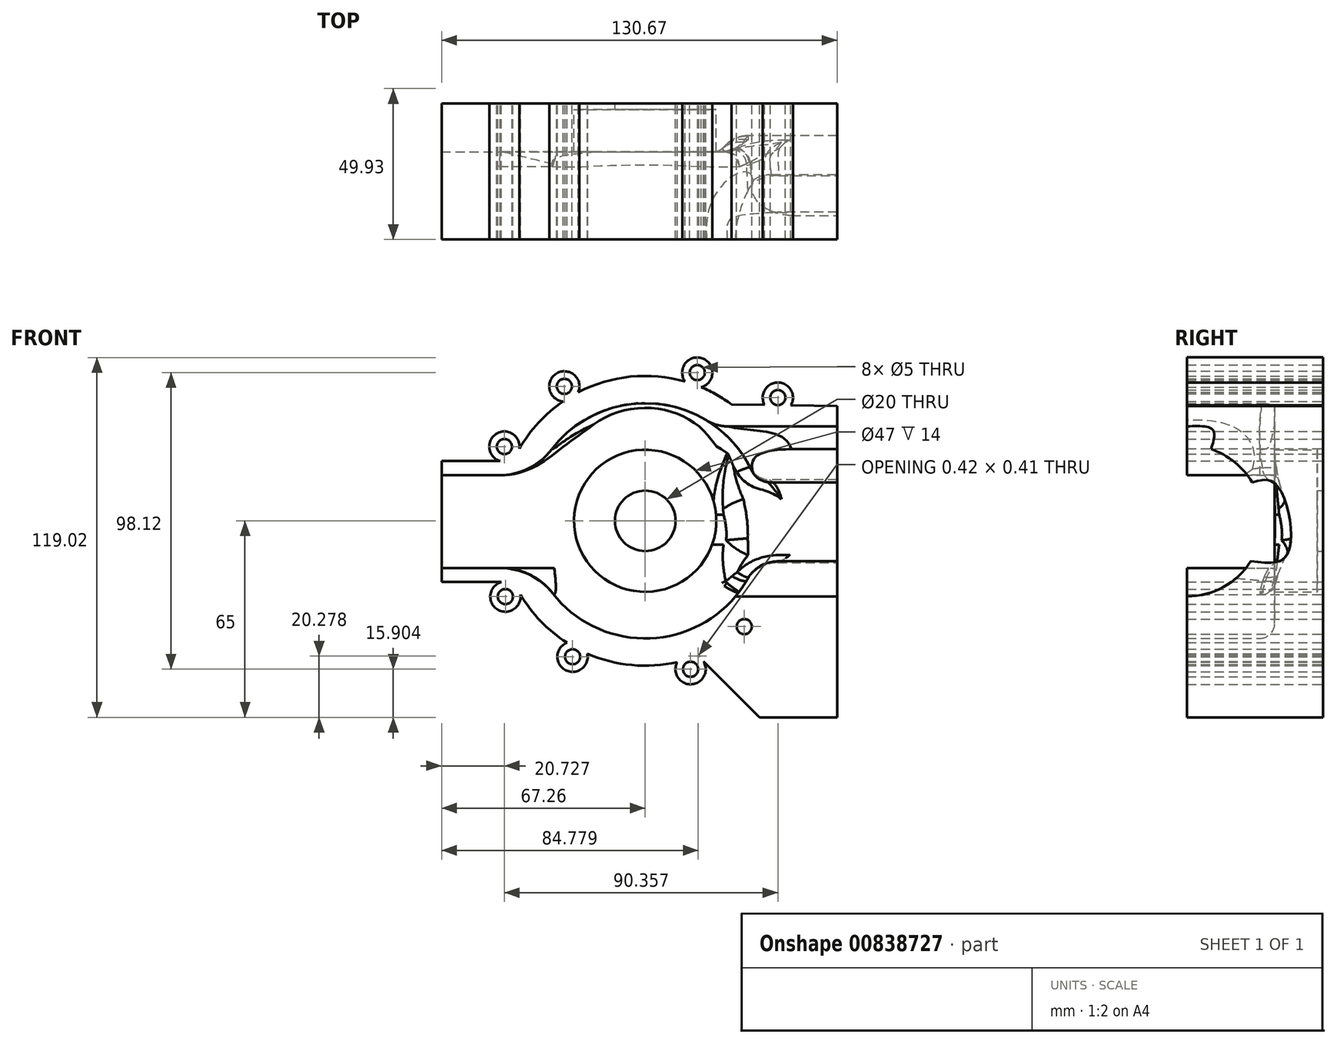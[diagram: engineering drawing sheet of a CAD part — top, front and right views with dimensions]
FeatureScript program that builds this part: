
annotation { "Feature Type Name" : "Feature", "Feature Type Description" : "" }
export const myFeature = defineFeature(function(context is Context, id is Id, definition is map)
    precondition{}
    {
        {
            var Q0;
            Q0=qCreatedBy(makeId("Front.planeOp"),FACE);
            var sketch = newSketch(context, id + "F0", { "sketchPlane" : qUnion([Q0])});
            skCircle(sketch, "E0", {"center": v(0, 0) * mm, "radius": 10 * mm});
            skCircle(sketch, "E1", {"center": v(0, 0) * mm, "radius": 23.5 * mm});
            skCircle(sketch, "E2", {"center": v(0, 0) * mm, "radius": 38.9 * mm});
            skLineSegment(sketch, "E3", {"start": v(-67.26, 19.74) * mm, "end": v(-33.52, 19.74) * mm});
            skLineSegment(sketch, "E4", {"start": v(-67.26, 19.74) * mm, "end": v(-67.26, -20.26) * mm});
            skLineSegment(sketch, "E5", {"start": v(-33.2, -20.26) * mm, "end": v(-67.26, -20.26) * mm});
            skArc(sketch, "E6", {"start": v(-43.42, -20.26) * mm, "mid": v(47.92, 0.28) * mm, "end": v(-43.66, 19.74) * mm});
            skLineSegment(sketch, "E7", {"start": v(-67.26, 15.06) * mm, "end": v(-35.87, 15.06) * mm});
            skLineSegment(sketch, "E8", {"start": v(-67.26, -15.65) * mm, "end": v(-35.61, -15.65) * mm});
            skLineSegment(sketch, "E9", {"start": v(28.53, 38.5) * mm, "end": v(63.41, 38) * mm});
            skLineSegment(sketch, "E10", {"start": v(63.41, 38) * mm, "end": v(63.41, -35) * mm});
            skLineSegment(sketch, "E11", {"start": v(63.41, -35) * mm, "end": v(32.73, -35) * mm});
            skLineSegment(sketch, "E12.bottom", {"start": v(28.66, 26.62) * mm, "end": v(63.41, 26.62) * mm});
            skLineSegment(sketch, "E12.top", {"start": v(31.09, -23.38) * mm, "end": v(63.41, -23.38) * mm});
            skLineSegment(sketch, "E12.left", {"start": v(28.66, 26.62) * mm, "end": v(28.66, 26.3) * mm});
            skPoint(sketch, "E12.middle", {"position": v(63.41, 1.5) * mm});
            skArc(sketch, "E13", {"start": v(-25.89, -40.32) * mm, "mid": v(-26.37, -49.37) * mm, "end": v(-19.12, -43.94) * mm});
            skArc(sketch, "E14", {"start": v(10.6, -46.73) * mm, "mid": v(16.45, -53.87) * mm, "end": v(17.3, -44.68) * mm});
            skArc(sketch, "E15", {"start": v(-47.54, -20.26) * mm, "mid": v(-48.95, -29.26) * mm, "end": v(-41.26, -24.37) * mm});
            skArc(sketch, "E16", {"start": v(-41.59, 23.8) * mm, "mid": v(-49.22, 28.76) * mm, "end": v(-47.95, 19.74) * mm});
            skArc(sketch, "E17", {"start": v(-22.12, 42.5) * mm, "mid": v(-29.3, 48.75) * mm, "end": v(-27.16, 39.47) * mm});
            skArc(sketch, "E18", {"start": v(18.5, 44.2) * mm, "mid": v(18.85, 53.74) * mm, "end": v(13.16, 46.07) * mm});
            skArc(sketch, "E19", {"start": v(48.14, 38.22) * mm, "mid": v(43.9, 45.75) * mm, "end": v(39.44, 38.34) * mm});
            skSolve(sketch);
        }
        {
            var Q0;
            Q0=makeQuery(id+"F0.imprint","IMPRINT",FACE,{"disambiguationData":[TD([[makeQuery(id+"F0.imprint","IMPRINT",EDGE,{"derivedFrom":sQuery(id+"F0.wireOp",EDGE,"E0")}),-1.0]])]});
            extrude(context, id + "F1", {"entities" : qUnion([Q0]), "depth" : 2 * mm, "offsetDistance" : 25 * mm});
        }
        {
            var Q0;
            Q0=makeQuery(id+"F0.imprint","IMPRINT",FACE,{"disambiguationData":[TD([[makeQuery(id+"F0.imprint","IMPRINT",EDGE,{"derivedFrom":sQuery(id+"F0.wireOp",EDGE,"E1")}),-1.0]])]});
            extrude(context, id + "F2", {"entities" : qUnion([Q0]), "operationType" : NewBodyOperationType.ADD, "depth" : 16 * mm, "offsetDistance" : 25 * mm});
        }
        {
            var Q0;
            {var subQ8=sQuery(id+"F0.wireOp",EDGE,"E12.left");Q0=makeQuery(id+"F0.imprint","IMPRINT",FACE,{"disambiguationData":[TD([[makeQuery(id+"F0.imprint","IMPRINT",EDGE,{"derivedFrom":subQ8}),-1.0]])]});}
            var Q1;
            {var subQ1=sQuery(id+"F0.wireOp",EDGE,"E5");var subQ4=sQuery(id+"F0.wireOp",EDGE,"E2");var subQ5=makeQuery(id+"F0.imprint","INTERSECT",VERTEX,{"derivedFrom":[subQ4,subQ1]});Q1=makeQuery(id+"F0.imprint","IMPRINT",FACE,{"disambiguationData":[TD([[makeQuery(id+"F0.imprint","IMPRINT",EDGE,{"disambiguationData":[TD([[subQ5,-1.0]])],"derivedFrom":subQ4}),-1.0]])]});}
            var Q2;
            {var subQ3=sQuery(id+"F0.wireOp",EDGE,"E7");Q2=makeQuery(id+"F0.imprint","IMPRINT",FACE,{"disambiguationData":[TD([[makeQuery(id+"F0.imprint","IMPRINT",EDGE,{"derivedFrom":subQ3}),1.0]])]});}
            var Q3;
            {var subQ6=sQuery(id+"F0.wireOp",EDGE,"E8");Q3=makeQuery(id+"F0.imprint","IMPRINT",FACE,{"disambiguationData":[TD([[makeQuery(id+"F0.imprint","IMPRINT",EDGE,{"derivedFrom":subQ6}),-1.0]])]});}
            var Q4;
            {var subQ0=sQuery(id+"F0.wireOp",EDGE,"E11");Q4=makeQuery(id+"F0.imprint","IMPRINT",FACE,{"disambiguationData":[TD([[makeQuery(id+"F0.imprint","IMPRINT",EDGE,{"derivedFrom":subQ0}),-1.0]])]});}
            var Q5;
            {var subQ0=sQuery(id+"F0.wireOp",EDGE,"E9");Q5=makeQuery(id+"F0.imprint","IMPRINT",FACE,{"disambiguationData":[TD([[makeQuery(id+"F0.imprint","IMPRINT",EDGE,{"derivedFrom":subQ0}),-1.0]])]});}
            extrude(context, id + "F3", {"entities" : qUnion([Q0, Q1, Q2, Q3, Q4, Q5]), "operationType" : NewBodyOperationType.ADD, "depth" : 35 * mm, "offsetDistance" : 25 * mm});
        }
        {
            var Q0;
            {var subQ0=sQuery(id+"F0.wireOp",EDGE,"E7");Q0=makeQuery(id+"F0.imprint","IMPRINT",FACE,{"disambiguationData":[TD([[makeQuery(id+"F0.imprint","IMPRINT",EDGE,{"derivedFrom":subQ0}),-1.0]])]});}
            var Q1;
            {var subQ0=sQuery(id+"F0.wireOp",EDGE,"E12.top");var subQ1=sQuery(id+"F0.wireOp",EDGE,"E6");var subQ2=makeQuery(id+"F0.imprint","INTERSECT",VERTEX,{"derivedFrom":[subQ1,subQ0]});Q1=makeQuery(id+"F0.imprint","IMPRINT",FACE,{"disambiguationData":[TD([[makeQuery(id+"F0.imprint","IMPRINT",EDGE,{"disambiguationData":[TD([[subQ2,-1.0]])],"derivedFrom":subQ1}),-1.0]])]});}
            var Q2;
            {var subQ5=sQuery(id+"F0.wireOp",EDGE,"E12.left");Q2=makeQuery(id+"F0.imprint","IMPRINT",FACE,{"disambiguationData":[TD([[makeQuery(id+"F0.imprint","IMPRINT",EDGE,{"derivedFrom":subQ5}),1.0]])]});}
            extrude(context, id + "F4", {"entities" : qUnion([Q0, Q1, Q2]), "operationType" : NewBodyOperationType.ADD, "depth" : 16 * mm, "offsetDistance" : 25 * mm});
        }
        {
            var Q0;
            Q0=makeQuery(id+"F3.opExtrude","SWEPT_FACE",FACE,{"disambiguationData":[OSD([sQuery(id+"F0.wireOp",EDGE,"E11")])]});
            extrude(context, id + "F5", {"entities" : qUnion([Q0]), "operationType" : NewBodyOperationType.ADD, "depth" : 30 * mm, "offsetDistance" : 25 * mm});
        }
        {
            var Q0;
            Q0=makeQuery(id+"F5.opExtrude","SWEPT_FACE",FACE,{"disambiguationData":[OSD([sQuery(id+"F0.wireOp",EDGE,"E6"),sQuery(id+"F0.wireOp",EDGE,"E11")])]});
            extrude(context, id + "F6", {"entities" : qUnion([Q0]), "operationType" : NewBodyOperationType.ADD, "depth" : 15 * mm, "offsetDistance" : 25 * mm});
        }
        {
            var Q0;
            {var subQ0=sQuery(id+"F0.wireOp",EDGE,"E11");var subQ1=sQuery(id+"F0.wireOp",EDGE,"E6");Q0=makeQuery(id+"F6.opExtrude","CAP_EDGE",EDGE,{"disambiguationData":[OSD([subQ1,subQ0]),TDD([makeQuery(id+"F5.opExtrude","CAP_EDGE",EDGE,{"disambiguationData":[OSD([subQ1,subQ0])],"isStart":false})])],"isStart":false});}
            chamfer(context, id + "F7", {"entities" : qUnion([Q0]), "width" : 20 * mm, "tangentPropagation" : true});
        }
        {
            var Q0;
            {var subQ5=sQuery(id+"F0.wireOp",EDGE,"E12.left");Q0=makeQuery(id+"F0.imprint","IMPRINT",FACE,{"disambiguationData":[TD([[makeQuery(id+"F0.imprint","IMPRINT",EDGE,{"derivedFrom":subQ5}),1.0]])]});}
            var Q1;
            {var subQ0=sQuery(id+"F0.wireOp",EDGE,"E12.top");var subQ1=sQuery(id+"F0.wireOp",EDGE,"E6");var subQ2=makeQuery(id+"F0.imprint","INTERSECT",VERTEX,{"derivedFrom":[subQ1,subQ0]});Q1=makeQuery(id+"F0.imprint","IMPRINT",FACE,{"disambiguationData":[TD([[makeQuery(id+"F0.imprint","IMPRINT",EDGE,{"disambiguationData":[TD([[subQ2,-1.0]])],"derivedFrom":subQ1}),-1.0]])]});}
            extrude(context, id + "F8", {"entities" : qUnion([Q0, Q1]), "operationType" : NewBodyOperationType.ADD, "depth" : 35 * mm, "offsetDistance" : 25 * mm});
        }
        {
            var Q0;
            {var subQ0=sQuery(id+"F0.wireOp",EDGE,"E12.left");var subQ1=sQuery(id+"F0.wireOp",EDGE,"E12.top");var subQ2=sQuery(id+"F0.wireOp",EDGE,"E12.bottom");var subQ3=sQuery(id+"F0.wireOp",EDGE,"E10");var subQ4=sQuery(id+"F0.wireOp",EDGE,"E2");var subQ5=sQuery(id+"F0.wireOp",EDGE,"E11");var subQ6=sQuery(id+"F0.wireOp",EDGE,"E6");var subQ7=sQuery(id+"F0.wireOp",EDGE,"E4");Q0=makeQuery(id+"F8.boolean.opBoolean","MERGE",FACE,{"derivedFrom":[makeQuery(id+"F3.opExtrude","CAP_FACE",FACE,{"disambiguationData":[OSD([subQ4,sQuery(id+"F0.wireOp",EDGE,"E3"),subQ7,subQ6,sQuery(id+"F0.wireOp",EDGE,"E7"),sQuery(id+"F0.wireOp",EDGE,"E9"),subQ3,subQ2,subQ0])],"isStart":false}),makeQuery(id+"F6.boolean.opBoolean","MERGE",FACE,{"derivedFrom":[makeQuery(id+"F5.boolean.opBoolean","MERGE",FACE,{"derivedFrom":[makeQuery(id+"F3.opExtrude","CAP_FACE",FACE,{"disambiguationData":[OSD([subQ4,subQ7,sQuery(id+"F0.wireOp",EDGE,"E5"),subQ6,sQuery(id+"F0.wireOp",EDGE,"E8"),subQ3,subQ5,subQ1])],"isStart":false}),makeQuery(id+"F5.opExtrude","SWEPT_FACE",FACE,{"disambiguationData":[OSD([subQ5]),TDD([makeQuery(id+"F3.opExtrude","CAP_EDGE",EDGE,{"disambiguationData":[OSD([subQ5])],"isStart":false})])]})]}),makeQuery(id+"F6.opExtrude","SWEPT_FACE",FACE,{"disambiguationData":[OSD([subQ6,subQ5]),TDD([makeQuery(id+"F5.opExtrude","SWEPT_EDGE",EDGE,{"disambiguationData":[OSD([subQ6,subQ5]),TDD([makeQuery(id+"F3.opExtrude","CAP_VERTEX",VERTEX,{"disambiguationData":[OSD([subQ6,subQ5])],"isStart":false})])]})])]})]}),makeQuery(id+"F8.opExtrude","CAP_FACE",FACE,{"disambiguationData":[OSD([subQ4,subQ3,subQ2,subQ1,subQ0])],"isStart":false})]});}
            extrude(context, id + "F9", {"entities" : qUnion([Q0]), "operationType" : NewBodyOperationType.ADD, "depth" : 10 * mm, "offsetDistance" : 25 * mm});
        }
        {
            var Q0;
            {var subQ0=sQuery(id+"F0.wireOp",EDGE,"E11");var subQ1=sQuery(id+"F0.wireOp",EDGE,"E10");Q0=makeQuery(id+"F9.boolean.opBoolean","MERGE",FACE,{"derivedFrom":[makeQuery(id+"F8.boolean.opBoolean","MERGE",FACE,{"derivedFrom":[makeQuery(id+"F5.boolean.opBoolean","MERGE",FACE,{"derivedFrom":[makeQuery(id+"F4.boolean.opBoolean","MERGE",FACE,{"derivedFrom":[makeQuery(id+"F3.opExtrude","SWEPT_FACE",FACE,{"disambiguationData":[OSD([subQ1]),TDD([makeQuery(id+"F0.imprint","IMPRINT",EDGE,{"disambiguationData":[TD([[makeQuery(id+"F0.imprint","INTERSECT",VERTEX,{"derivedFrom":[sQuery(id+"F0.wireOp",EDGE,"E9"),subQ1]}),-1.0]])],"derivedFrom":subQ1})])]}),makeQuery(id+"F3.opExtrude","SWEPT_FACE",FACE,{"disambiguationData":[OSD([subQ1]),TDD([makeQuery(id+"F0.imprint","IMPRINT",EDGE,{"disambiguationData":[TD([[makeQuery(id+"F0.imprint","INTERSECT",VERTEX,{"derivedFrom":[subQ1,subQ0]}),1.0]])],"derivedFrom":subQ1})])]}),makeQuery(id+"F4.opExtrude","SWEPT_FACE",FACE,{"disambiguationData":[OSD([subQ1])]})]}),makeQuery(id+"F5.opExtrude","SWEPT_FACE",FACE,{"disambiguationData":[OSD([subQ1,subQ0])]})]}),makeQuery(id+"F8.opExtrude","SWEPT_FACE",FACE,{"disambiguationData":[OSD([subQ1])]})]}),makeQuery(id+"F9.opExtrude","SWEPT_FACE",FACE,{"disambiguationData":[OSD([subQ1,subQ0])]})]});}
            var sketch = newSketch(context, id + "F10", { "sketchPlane" : qUnion([Q0])});
            skArc(sketch, "E20", {"start": v(-23.46, 12.69) * mm, "mid": v(-32.6, 21.7) * mm, "end": v(-45, 25) * mm});
            skFitSpline(sketch, "E21", {"points": [v(-23.46, 12.69) * mm, v(-16.54, 12.88) * mm, v(-11, 0) * mm, v(-12.98, -12.48) * mm, v(-23.87, -13.36) * mm], "startDerivative": vector(40.87, 11.17) * mm, "endDerivative": vector(-55.8, 6.66) * mm});
            skFitSpline(sketch, "E22", {"points": [v(-37.04, 23.7) * mm, v(-36.44, 30.03) * mm, v(-45, 31.24) * mm], "startDerivative": vector(5.27, 16.32) * mm, "endDerivative": vector(-20.53, -0.83) * mm});
            skLineSegment(sketch, "E23", {"start": v(-45, 31.24) * mm, "end": v(-45, 25) * mm});
            skArc(sketch, "E24", {"start": v(-45, -25) * mm, "mid": v(-20, 0) * mm, "end": v(-45, 25) * mm});
            skLineSegment(sketch, "E25", {"start": v(-45, 25) * mm, "end": v(-45, -25) * mm});
            skArc(sketch, "E26.trimOffspring", {"start": v(-45, -25) * mm, "mid": v(-32.94, -21.9) * mm, "end": v(-23.87, -13.36) * mm});
            skSolve(sketch);
        }
        {
            var Q0;
            {var subQ0=sQuery(id+"F10.wireOp",EDGE,"E25");Q0=makeQuery(id+"F10.imprint","IMPRINT",FACE,{"disambiguationData":[TD([[makeQuery(id+"F10.imprint","IMPRINT",EDGE,{"derivedFrom":subQ0}),1.0]])]});}
            extrude(context, id + "F11", {"entities" : qUnion([Q0]), "operationType" : NewBodyOperationType.REMOVE, "oppositeDirection" : true, "depth" : 51.1 * mm, "offsetDistance" : 25 * mm});
        }
        {
            var Q0;
            {var subQ0=sQuery(id+"F10.wireOp",EDGE,"E21");Q0=makeQuery(id+"F10.imprint","IMPRINT",FACE,{"disambiguationData":[TD([[makeQuery(id+"F10.imprint","IMPRINT",EDGE,{"derivedFrom":subQ0}),-1.0]])]});}
            var Q1;
            {var subQ0=sQuery(id+"F10.wireOp",EDGE,"E22");Q1=makeQuery(id+"F10.imprint","IMPRINT",FACE,{"disambiguationData":[TD([[makeQuery(id+"F10.imprint","IMPRINT",EDGE,{"derivedFrom":subQ0}),1.0]])]});}
            extrude(context, id + "F12", {"entities" : qUnion([Q0, Q1]), "operationType" : NewBodyOperationType.REMOVE, "oppositeDirection" : true, "depth" : 34 * mm, "offsetDistance" : 25 * mm});
        }
        {
            var Q0;
            Q0=makeQuery(id+"F12.boolean.opBoolean","COPY",FACE,{"derivedFrom":makeQuery(id+"F12.opExtrude","CAP_FACE",FACE,{"disambiguationData":[OSD([sQuery(id+"F10.wireOp",EDGE,"E22"),sQuery(id+"F10.wireOp",EDGE,"E23"),sQuery(id+"F10.wireOp",EDGE,"E24")])],"isStart":false})});
            extrude(context, id + "F13", {"entities" : qUnion([Q0]), "operationType" : NewBodyOperationType.REMOVE, "oppositeDirection" : true, "depth" : 25 * mm, "offsetDistance" : 25 * mm});
        }
        {
            var Q0;
            {var subQ0=sQuery(id+"F0.wireOp",EDGE,"E2");Q0=makeQuery(id+"F12.boolean.opBoolean","INTERSECT",EDGE,{"disambiguationData":[OD(0.0)],"derivedFrom":[makeQuery(id+"F4.boolean.opBoolean","MERGE",FACE,{"derivedFrom":[makeQuery(id+"F2.opExtrude","CAP_FACE",FACE,{"disambiguationData":[OSD([sQuery(id+"F0.wireOp",EDGE,"E1"),subQ0])],"isStart":false}),makeQuery(id+"F4.opExtrude","CAP_FACE",FACE,{"disambiguationData":[OSD([subQ0,sQuery(id+"F0.wireOp",EDGE,"E4"),sQuery(id+"F0.wireOp",EDGE,"E7"),sQuery(id+"F0.wireOp",EDGE,"E8")])],"isStart":false}),makeQuery(id+"F4.opExtrude","CAP_FACE",FACE,{"disambiguationData":[OSD([subQ0,sQuery(id+"F0.wireOp",EDGE,"E10"),sQuery(id+"F0.wireOp",EDGE,"E12.bottom"),sQuery(id+"F0.wireOp",EDGE,"E12.top"),sQuery(id+"F0.wireOp",EDGE,"E12.left")])],"isStart":false})]}),makeQuery(id+"F12.opExtrude","SWEPT_FACE",FACE,{"disambiguationData":[OSD([sQuery(id+"F10.wireOp",EDGE,"E21")])]})]});}
            fillet(context, id + "F14", {"entities" : qUnion([Q0]), "radius" : 50.43 * mm, "tangentPropagation" : true, "allowEdgeOverflow" : false});
        }
        {
            var Q0;
            {var subQ0=sQuery(id+"F0.wireOp",EDGE,"E2");Q0=makeQuery(id+"F12.boolean.opBoolean","INTERSECT",EDGE,{"disambiguationData":[OD(1.0)],"derivedFrom":[makeQuery(id+"F4.boolean.opBoolean","MERGE",FACE,{"derivedFrom":[makeQuery(id+"F2.opExtrude","CAP_FACE",FACE,{"disambiguationData":[OSD([sQuery(id+"F0.wireOp",EDGE,"E1"),subQ0])],"isStart":false}),makeQuery(id+"F4.opExtrude","CAP_FACE",FACE,{"disambiguationData":[OSD([subQ0,sQuery(id+"F0.wireOp",EDGE,"E4"),sQuery(id+"F0.wireOp",EDGE,"E7"),sQuery(id+"F0.wireOp",EDGE,"E8")])],"isStart":false}),makeQuery(id+"F4.opExtrude","CAP_FACE",FACE,{"disambiguationData":[OSD([subQ0,sQuery(id+"F0.wireOp",EDGE,"E10"),sQuery(id+"F0.wireOp",EDGE,"E12.bottom"),sQuery(id+"F0.wireOp",EDGE,"E12.top"),sQuery(id+"F0.wireOp",EDGE,"E12.left")])],"isStart":false})]}),makeQuery(id+"F12.opExtrude","SWEPT_FACE",FACE,{"disambiguationData":[OSD([sQuery(id+"F10.wireOp",EDGE,"E21")])]})]});}
            fillet(context, id + "F15", {"entities" : qUnion([Q0]), "radius" : 27.1 * mm, "tangentPropagation" : true, "allowEdgeOverflow" : false});
        }
        {
            var Q0;
            {var subQ0=sQuery(id+"F0.wireOp",EDGE,"E2");Q0=makeQuery(id+"F12.boolean.opBoolean","INTERSECT",EDGE,{"derivedFrom":[makeQuery(id+"F4.boolean.opBoolean","MERGE",FACE,{"derivedFrom":[makeQuery(id+"F2.opExtrude","CAP_FACE",FACE,{"disambiguationData":[OSD([sQuery(id+"F0.wireOp",EDGE,"E1"),subQ0])],"isStart":false}),makeQuery(id+"F4.opExtrude","CAP_FACE",FACE,{"disambiguationData":[OSD([subQ0,sQuery(id+"F0.wireOp",EDGE,"E4"),sQuery(id+"F0.wireOp",EDGE,"E7"),sQuery(id+"F0.wireOp",EDGE,"E8")])],"isStart":false}),makeQuery(id+"F4.opExtrude","CAP_FACE",FACE,{"disambiguationData":[OSD([subQ0,sQuery(id+"F0.wireOp",EDGE,"E10"),sQuery(id+"F0.wireOp",EDGE,"E12.bottom"),sQuery(id+"F0.wireOp",EDGE,"E12.top"),sQuery(id+"F0.wireOp",EDGE,"E12.left")])],"isStart":false})]}),makeQuery(id+"F12.opExtrude","CAP_FACE",FACE,{"disambiguationData":[OSD([sQuery(id+"F10.wireOp",EDGE,"E21"),sQuery(id+"F10.wireOp",EDGE,"E24")])],"isStart":false})]});}
            chamfer(context, id + "F16", {"entities" : qUnion([Q0]), "width" : 5 * mm, "tangentPropagation" : true});
        }
        {
            var Q0;
            {var subQ0=sQuery(id+"F10.wireOp",EDGE,"E21");var subQ1=sQuery(id+"F0.wireOp",EDGE,"E12.left");var subQ2=sQuery(id+"F0.wireOp",EDGE,"E12.top");var subQ3=sQuery(id+"F0.wireOp",EDGE,"E12.bottom");var subQ4=sQuery(id+"F0.wireOp",EDGE,"E10");var subQ5=sQuery(id+"F0.wireOp",EDGE,"E8");var subQ6=sQuery(id+"F0.wireOp",EDGE,"E7");var subQ7=sQuery(id+"F0.wireOp",EDGE,"E4");var subQ8=sQuery(id+"F0.wireOp",EDGE,"E2");var subQ9=sQuery(id+"F0.wireOp",EDGE,"E1");Q0=makeQuery(id+"F16.opChamfer","BLEND_EDGE",EDGE,{"blendedFrom":[makeQuery(id+"F12.boolean.opBoolean","INTERSECT",EDGE,{"derivedFrom":[makeQuery(id+"F4.boolean.opBoolean","MERGE",FACE,{"derivedFrom":[makeQuery(id+"F2.opExtrude","CAP_FACE",FACE,{"disambiguationData":[OSD([subQ9,subQ8])],"isStart":false}),makeQuery(id+"F4.opExtrude","CAP_FACE",FACE,{"disambiguationData":[OSD([subQ8,subQ7,subQ6,subQ5])],"isStart":false}),makeQuery(id+"F4.opExtrude","CAP_FACE",FACE,{"disambiguationData":[OSD([subQ8,subQ4,subQ3,subQ2,subQ1])],"isStart":false})]}),makeQuery(id+"F12.opExtrude","CAP_FACE",FACE,{"disambiguationData":[OSD([subQ0,sQuery(id+"F10.wireOp",EDGE,"E24")])],"isStart":false})]}),makeQuery(id+"F15.opFillet","BLEND_FACE",FACE,{"disambiguationData":[OSD([subQ9,subQ8,subQ7,subQ6,subQ5,subQ4,subQ3,subQ2,subQ1,subQ0])]})],"blendedInto":[makeQuery(id+"F15.opFillet","BLEND_FACE",FACE,{"disambiguationData":[OSD([subQ9,subQ8,subQ7,subQ6,subQ5,subQ4,subQ3,subQ2,subQ1,subQ0])]})]});}
            fillet(context, id + "F17", {"entities" : qUnion([Q0]), "radius" : 10 * mm, "tangentPropagation" : true, "allowEdgeOverflow" : false});
        }
        {
            var Q0;
            {var subQ0=sQuery(id+"F0.wireOp",EDGE,"E18");Q0=makeQuery(id+"F0.imprint","IMPRINT",FACE,{"disambiguationData":[TD([[makeQuery(id+"F0.imprint","IMPRINT",EDGE,{"derivedFrom":subQ0}),1.0]])]});}
            var Q1;
            {var subQ0=sQuery(id+"F0.wireOp",EDGE,"E17");Q1=makeQuery(id+"F0.imprint","IMPRINT",FACE,{"disambiguationData":[TD([[makeQuery(id+"F0.imprint","IMPRINT",EDGE,{"derivedFrom":subQ0}),1.0]])]});}
            var Q2;
            {var subQ3=sQuery(id+"F0.wireOp",EDGE,"E16");Q2=makeQuery(id+"F0.imprint","IMPRINT",FACE,{"disambiguationData":[TD([[makeQuery(id+"F0.imprint","IMPRINT",EDGE,{"derivedFrom":subQ3}),1.0]])]});}
            var Q3;
            {var subQ3=sQuery(id+"F0.wireOp",EDGE,"E15");Q3=makeQuery(id+"F0.imprint","IMPRINT",FACE,{"disambiguationData":[TD([[makeQuery(id+"F0.imprint","IMPRINT",EDGE,{"derivedFrom":subQ3}),1.0]])]});}
            var Q4;
            {var subQ0=sQuery(id+"F0.wireOp",EDGE,"E13");Q4=makeQuery(id+"F0.imprint","IMPRINT",FACE,{"disambiguationData":[TD([[makeQuery(id+"F0.imprint","IMPRINT",EDGE,{"derivedFrom":subQ0}),1.0]])]});}
            var Q5;
            {var subQ0=sQuery(id+"F0.wireOp",EDGE,"E14");Q5=makeQuery(id+"F0.imprint","IMPRINT",FACE,{"disambiguationData":[TD([[makeQuery(id+"F0.imprint","IMPRINT",EDGE,{"derivedFrom":subQ0}),1.0]])]});}
            extrude(context, id + "F18", {"entities" : qUnion([Q0, Q1, Q2, Q3, Q4, Q5]), "operationType" : NewBodyOperationType.ADD, "depth" : 45 * mm, "offsetDistance" : 25 * mm});
        }
        {
            var Q0;
            Q0=sQuery(id+"F0.wireOp",VERTEX,"E16.center");
            var Q1;
            Q1=sQuery(id+"F0.wireOp",VERTEX,"E17.center");
            var Q2;
            Q2=sQuery(id+"F0.wireOp",VERTEX,"E18.center");
            var Q3;
            Q3=sQuery(id+"F0.wireOp",VERTEX,"E19.center");
            var Q4;
            Q4=sQuery(id+"F0.wireOp",VERTEX,"E11.end");
            var Q5;
            Q5=sQuery(id+"F0.wireOp",VERTEX,"E14.center");
            var Q6;
            Q6=sQuery(id+"F0.wireOp",VERTEX,"E13.center");
            var Q7;
            Q7=sQuery(id+"F0.wireOp",VERTEX,"E15.center");
            var Q8;
            Q8=makeQuery(id+"F1.opExtrude","SWEPT_BODY",BODY,{"disambiguationData":[OSD([sQuery(id+"F0.wireOp",EDGE,"E0"),sQuery(id+"F0.wireOp",EDGE,"E1")])]});
            hole(context, id + "F19", {"style" : HoleStyle.SIMPLE, "endStyle" : HoleEndStyle.THROUGH, "oppositeDirection" : true, "holeDiameter" : 5 * mm, "majorDiameter" : 5 * mm, "isTappedThrough" : true, "tappedDepth" : 12 * mm, "tapClearance" : 3, "locations" : qUnion([Q0, Q1, Q2, Q3, Q4, Q5, Q6, Q7]), "scope" : qUnion([Q8])});
        }
        {
            var Q0;
            {var subQ0=sQuery(id+"F0.wireOp",EDGE,"E19");Q0=makeQuery(id+"F0.imprint","IMPRINT",FACE,{"disambiguationData":[TD([[makeQuery(id+"F0.imprint","IMPRINT",EDGE,{"derivedFrom":subQ0}),1.0]])]});}
            extrude(context, id + "F20", {"entities" : qUnion([Q0]), "operationType" : NewBodyOperationType.ADD, "depth" : 45 * mm, "offsetDistance" : 25 * mm});
        }
        {
            var Q0;
            Q0=sQuery(id+"F0.wireOp",VERTEX,"E19.center");
            var Q1;
            Q1=makeQuery(id+"F1.opExtrude","SWEPT_BODY",BODY,{"disambiguationData":[OSD([sQuery(id+"F0.wireOp",EDGE,"E0"),sQuery(id+"F0.wireOp",EDGE,"E1")])]});
            hole(context, id + "F21", {"style" : HoleStyle.SIMPLE, "endStyle" : HoleEndStyle.THROUGH, "oppositeDirection" : true, "holeDiameter" : 5 * mm, "majorDiameter" : 5 * mm, "isTappedThrough" : true, "tappedDepth" : 12 * mm, "tapClearance" : 3, "locations" : qUnion([Q0]), "scope" : qUnion([Q1])});
        }
        {
            var Q0;
            {var subQ0=sQuery(id+"F0.wireOp",EDGE,"E2");var subQ1=makeQuery(id+"F0.imprint","INTERSECT",VERTEX,{"derivedFrom":[subQ0,sQuery(id+"F0.wireOp",EDGE,"E5")]});var subQ2=makeQuery(id+"F0.imprint","INTERSECT",VERTEX,{"derivedFrom":[subQ0,sQuery(id+"F0.wireOp",EDGE,"E3")]});Q0=makeQuery(id+"F12.boolean.opBoolean","INTERSECT",EDGE,{"disambiguationData":[OD(1.0)],"derivedFrom":[makeQuery(id+"F9.boolean.opBoolean","MERGE",FACE,{"derivedFrom":[makeQuery(id+"F8.boolean.opBoolean","MERGE",FACE,{"derivedFrom":[makeQuery(id+"F3.opExtrude","SWEPT_FACE",FACE,{"disambiguationData":[OSD([subQ0]),TDD([makeQuery(id+"F0.imprint","IMPRINT",EDGE,{"disambiguationData":[TD([[subQ2,1.0]])],"derivedFrom":subQ0}),makeQuery(id+"F0.imprint","IMPRINT",EDGE,{"disambiguationData":[TD([[subQ2,-1.0]])],"derivedFrom":subQ0})])]}),makeQuery(id+"F3.opExtrude","SWEPT_FACE",FACE,{"disambiguationData":[OSD([subQ0]),TDD([makeQuery(id+"F0.imprint","IMPRINT",EDGE,{"disambiguationData":[TD([[subQ1,1.0]])],"derivedFrom":subQ0}),makeQuery(id+"F0.imprint","IMPRINT",EDGE,{"disambiguationData":[TD([[subQ1,-1.0]])],"derivedFrom":subQ0})])]}),makeQuery(id+"F8.opExtrude","SWEPT_FACE",FACE,{"disambiguationData":[OSD([subQ0])]})]}),makeQuery(id+"F9.opExtrude","SWEPT_FACE",FACE,{"disambiguationData":[OSD([subQ0])]})]}),makeQuery(id+"F12.opExtrude","SWEPT_FACE",FACE,{"disambiguationData":[OSD([sQuery(id+"F10.wireOp",EDGE,"E21")])]})]});}
            fillet(context, id + "F22", {"entities" : qUnion([Q0]), "radius" : 12 * mm, "tangentPropagation" : true, "allowEdgeOverflow" : false});
        }
        {
            var Q0;
            {var subQ0=sQuery(id+"F0.wireOp",EDGE,"E2");var subQ1=makeQuery(id+"F0.imprint","INTERSECT",VERTEX,{"derivedFrom":[subQ0,sQuery(id+"F0.wireOp",EDGE,"E5")]});var subQ2=makeQuery(id+"F0.imprint","INTERSECT",VERTEX,{"derivedFrom":[subQ0,sQuery(id+"F0.wireOp",EDGE,"E3")]});Q0=makeQuery(id+"F12.boolean.opBoolean","INTERSECT",EDGE,{"disambiguationData":[OD(0.0)],"derivedFrom":[makeQuery(id+"F9.boolean.opBoolean","MERGE",FACE,{"derivedFrom":[makeQuery(id+"F8.boolean.opBoolean","MERGE",FACE,{"derivedFrom":[makeQuery(id+"F3.opExtrude","SWEPT_FACE",FACE,{"disambiguationData":[OSD([subQ0]),TDD([makeQuery(id+"F0.imprint","IMPRINT",EDGE,{"disambiguationData":[TD([[subQ2,1.0]])],"derivedFrom":subQ0}),makeQuery(id+"F0.imprint","IMPRINT",EDGE,{"disambiguationData":[TD([[subQ2,-1.0]])],"derivedFrom":subQ0})])]}),makeQuery(id+"F3.opExtrude","SWEPT_FACE",FACE,{"disambiguationData":[OSD([subQ0]),TDD([makeQuery(id+"F0.imprint","IMPRINT",EDGE,{"disambiguationData":[TD([[subQ1,1.0]])],"derivedFrom":subQ0}),makeQuery(id+"F0.imprint","IMPRINT",EDGE,{"disambiguationData":[TD([[subQ1,-1.0]])],"derivedFrom":subQ0})])]}),makeQuery(id+"F8.opExtrude","SWEPT_FACE",FACE,{"disambiguationData":[OSD([subQ0])]})]}),makeQuery(id+"F9.opExtrude","SWEPT_FACE",FACE,{"disambiguationData":[OSD([subQ0])]})]}),makeQuery(id+"F12.opExtrude","SWEPT_FACE",FACE,{"disambiguationData":[OSD([sQuery(id+"F10.wireOp",EDGE,"E21")])]})]});}
            fillet(context, id + "F23", {"entities" : qUnion([Q0]), "radius" : 7.2 * mm, "tangentPropagation" : true, "allowEdgeOverflow" : false});
        }
        {
            var Q0;
            {var subQ0=sQuery(id+"F10.wireOp",EDGE,"E21");var subQ1=sQuery(id+"F0.wireOp",EDGE,"E12.left");var subQ2=sQuery(id+"F0.wireOp",EDGE,"E12.top");var subQ3=sQuery(id+"F0.wireOp",EDGE,"E8");var subQ4=sQuery(id+"F0.wireOp",EDGE,"E7");var subQ5=sQuery(id+"F0.wireOp",EDGE,"E2");var subQ6=makeQuery(id+"F0.imprint","INTERSECT",VERTEX,{"derivedFrom":[subQ5,sQuery(id+"F0.wireOp",EDGE,"E5")]});var subQ7=makeQuery(id+"F0.imprint","INTERSECT",VERTEX,{"derivedFrom":[subQ5,sQuery(id+"F0.wireOp",EDGE,"E3")]});Q0=makeQuery(id+"F23.opFillet","BLEND_EDGE",EDGE,{"blendedFrom":[makeQuery(id+"F12.boolean.opBoolean","INTERSECT",EDGE,{"disambiguationData":[OD(0.0)],"derivedFrom":[makeQuery(id+"F9.boolean.opBoolean","MERGE",FACE,{"derivedFrom":[makeQuery(id+"F8.boolean.opBoolean","MERGE",FACE,{"derivedFrom":[makeQuery(id+"F3.opExtrude","SWEPT_FACE",FACE,{"disambiguationData":[OSD([subQ5]),TDD([makeQuery(id+"F0.imprint","IMPRINT",EDGE,{"disambiguationData":[TD([[subQ7,1.0]])],"derivedFrom":subQ5}),makeQuery(id+"F0.imprint","IMPRINT",EDGE,{"disambiguationData":[TD([[subQ7,-1.0]])],"derivedFrom":subQ5})])]}),makeQuery(id+"F3.opExtrude","SWEPT_FACE",FACE,{"disambiguationData":[OSD([subQ5]),TDD([makeQuery(id+"F0.imprint","IMPRINT",EDGE,{"disambiguationData":[TD([[subQ6,1.0]])],"derivedFrom":subQ5}),makeQuery(id+"F0.imprint","IMPRINT",EDGE,{"disambiguationData":[TD([[subQ6,-1.0]])],"derivedFrom":subQ5})])]}),makeQuery(id+"F8.opExtrude","SWEPT_FACE",FACE,{"disambiguationData":[OSD([subQ5])]})]}),makeQuery(id+"F9.opExtrude","SWEPT_FACE",FACE,{"disambiguationData":[OSD([subQ5])]})]}),makeQuery(id+"F12.opExtrude","SWEPT_FACE",FACE,{"disambiguationData":[OSD([subQ0])]})]}),makeQuery(id+"F14.opFillet","BLEND_FACE",FACE,{"disambiguationData":[OSD([sQuery(id+"F0.wireOp",EDGE,"E1"),subQ5,sQuery(id+"F0.wireOp",EDGE,"E4"),subQ4,subQ3,sQuery(id+"F0.wireOp",EDGE,"E10"),sQuery(id+"F0.wireOp",EDGE,"E12.bottom"),subQ2,subQ1,subQ0])]})],"blendedInto":[makeQuery(id+"F14.opFillet","BLEND_FACE",FACE,{"disambiguationData":[OSD([sQuery(id+"F0.wireOp",EDGE,"E1"),subQ5,sQuery(id+"F0.wireOp",EDGE,"E4"),subQ4,subQ3,sQuery(id+"F0.wireOp",EDGE,"E10"),sQuery(id+"F0.wireOp",EDGE,"E12.bottom"),subQ2,subQ1,subQ0])]})]});}
            fillet(context, id + "F24", {"entities" : qUnion([Q0]), "radius" : 5 * mm, "tangentPropagation" : true, "rho" : 0.5, "crossSection" : FilletCrossSection.CONIC, "allowEdgeOverflow" : false});
        }
        {
            var Q0;
            {var subQ0=sQuery(id+"F10.wireOp",EDGE,"E21");var subQ1=sQuery(id+"F0.wireOp",EDGE,"E12.left");var subQ2=sQuery(id+"F0.wireOp",EDGE,"E12.top");var subQ3=sQuery(id+"F0.wireOp",EDGE,"E8");var subQ4=sQuery(id+"F0.wireOp",EDGE,"E7");var subQ5=sQuery(id+"F0.wireOp",EDGE,"E2");var subQ6=makeQuery(id+"F0.imprint","INTERSECT",VERTEX,{"derivedFrom":[subQ5,sQuery(id+"F0.wireOp",EDGE,"E5")]});var subQ7=makeQuery(id+"F0.imprint","INTERSECT",VERTEX,{"derivedFrom":[subQ5,sQuery(id+"F0.wireOp",EDGE,"E3")]});Q0=makeQuery(id+"F22.opFillet","BLEND_EDGE",EDGE,{"blendedFrom":[makeQuery(id+"F12.boolean.opBoolean","INTERSECT",EDGE,{"disambiguationData":[OD(1.0)],"derivedFrom":[makeQuery(id+"F9.boolean.opBoolean","MERGE",FACE,{"derivedFrom":[makeQuery(id+"F8.boolean.opBoolean","MERGE",FACE,{"derivedFrom":[makeQuery(id+"F3.opExtrude","SWEPT_FACE",FACE,{"disambiguationData":[OSD([subQ5]),TDD([makeQuery(id+"F0.imprint","IMPRINT",EDGE,{"disambiguationData":[TD([[subQ7,1.0]])],"derivedFrom":subQ5}),makeQuery(id+"F0.imprint","IMPRINT",EDGE,{"disambiguationData":[TD([[subQ7,-1.0]])],"derivedFrom":subQ5})])]}),makeQuery(id+"F3.opExtrude","SWEPT_FACE",FACE,{"disambiguationData":[OSD([subQ5]),TDD([makeQuery(id+"F0.imprint","IMPRINT",EDGE,{"disambiguationData":[TD([[subQ6,1.0]])],"derivedFrom":subQ5}),makeQuery(id+"F0.imprint","IMPRINT",EDGE,{"disambiguationData":[TD([[subQ6,-1.0]])],"derivedFrom":subQ5})])]}),makeQuery(id+"F8.opExtrude","SWEPT_FACE",FACE,{"disambiguationData":[OSD([subQ5])]})]}),makeQuery(id+"F9.opExtrude","SWEPT_FACE",FACE,{"disambiguationData":[OSD([subQ5])]})]}),makeQuery(id+"F12.opExtrude","SWEPT_FACE",FACE,{"disambiguationData":[OSD([subQ0])]})]}),makeQuery(id+"F15.opFillet","BLEND_FACE",FACE,{"disambiguationData":[OSD([sQuery(id+"F0.wireOp",EDGE,"E1"),subQ5,sQuery(id+"F0.wireOp",EDGE,"E4"),subQ4,subQ3,sQuery(id+"F0.wireOp",EDGE,"E10"),sQuery(id+"F0.wireOp",EDGE,"E12.bottom"),subQ2,subQ1,subQ0])]})],"blendedInto":[makeQuery(id+"F15.opFillet","BLEND_FACE",FACE,{"disambiguationData":[OSD([sQuery(id+"F0.wireOp",EDGE,"E1"),subQ5,sQuery(id+"F0.wireOp",EDGE,"E4"),subQ4,subQ3,sQuery(id+"F0.wireOp",EDGE,"E10"),sQuery(id+"F0.wireOp",EDGE,"E12.bottom"),subQ2,subQ1,subQ0])]})]});}
            fillet(context, id + "F25", {"entities" : qUnion([Q0]), "radius" : 5 * mm, "tangentPropagation" : true, "allowEdgeOverflow" : false});
        }
        {
            var Q0;
            {var subQ0=sQuery(id+"F0.wireOp",EDGE,"E8");var subQ1=sQuery(id+"F0.wireOp",EDGE,"E2");var subQ2=makeQuery(id+"F0.imprint","INTERSECT",VERTEX,{"derivedFrom":[subQ1,sQuery(id+"F0.wireOp",EDGE,"E5")]});Q0=makeQuery(id+"F9.boolean.opBoolean","MERGE",EDGE,{"derivedFrom":[makeQuery(id+"F3.boolean.opBoolean","SPLIT",EDGE,{"disambiguationData":[topologyDisambiguationEdgeConnected([makeQuery(id+"F3.opExtrude","SWEPT_FACE",FACE,{"disambiguationData":[OSD([subQ1]),TDD([makeQuery(id+"F0.imprint","IMPRINT",EDGE,{"disambiguationData":[TD([[subQ2,1.0]])],"derivedFrom":subQ1}),makeQuery(id+"F0.imprint","IMPRINT",EDGE,{"disambiguationData":[TD([[subQ2,-1.0]])],"derivedFrom":subQ1})])]})])],"derivedFrom":makeQuery(id+"F3.opExtrude","SWEPT_EDGE",EDGE,{"disambiguationData":[OSD([subQ1,subQ0])]})}),makeQuery(id+"F9.opExtrude","SWEPT_EDGE",EDGE,{"disambiguationData":[OSD([subQ1,subQ0])]})]});}
            var Q1;
            {var subQ0=sQuery(id+"F0.wireOp",EDGE,"E7");var subQ1=sQuery(id+"F0.wireOp",EDGE,"E2");var subQ2=makeQuery(id+"F0.imprint","INTERSECT",VERTEX,{"derivedFrom":[subQ1,sQuery(id+"F0.wireOp",EDGE,"E3")]});Q1=makeQuery(id+"F9.boolean.opBoolean","MERGE",EDGE,{"derivedFrom":[makeQuery(id+"F3.boolean.opBoolean","SPLIT",EDGE,{"disambiguationData":[topologyDisambiguationEdgeConnected([makeQuery(id+"F3.opExtrude","SWEPT_FACE",FACE,{"disambiguationData":[OSD([subQ1]),TDD([makeQuery(id+"F0.imprint","IMPRINT",EDGE,{"disambiguationData":[TD([[subQ2,1.0]])],"derivedFrom":subQ1}),makeQuery(id+"F0.imprint","IMPRINT",EDGE,{"disambiguationData":[TD([[subQ2,-1.0]])],"derivedFrom":subQ1})])]})])],"derivedFrom":makeQuery(id+"F3.opExtrude","SWEPT_EDGE",EDGE,{"disambiguationData":[OSD([subQ1,subQ0])]})}),makeQuery(id+"F9.opExtrude","SWEPT_EDGE",EDGE,{"disambiguationData":[OSD([subQ1,subQ0])]})]});}
            fillet(context, id + "F26", {"entities" : qUnion([Q0, Q1]), "radius" : 21.91 * mm, "tangentPropagation" : true, "allowEdgeOverflow" : false});
        }
        {
            var Q0;
            {var subQ0=sQuery(id+"F0.wireOp",EDGE,"E2");var subQ1=makeQuery(id+"F4.boolean.opBoolean","MERGE",FACE,{"derivedFrom":[makeQuery(id+"F2.opExtrude","CAP_FACE",FACE,{"disambiguationData":[OSD([sQuery(id+"F0.wireOp",EDGE,"E1"),subQ0])],"isStart":false}),makeQuery(id+"F4.opExtrude","CAP_FACE",FACE,{"disambiguationData":[OSD([subQ0,sQuery(id+"F0.wireOp",EDGE,"E4"),sQuery(id+"F0.wireOp",EDGE,"E7"),sQuery(id+"F0.wireOp",EDGE,"E8")])],"isStart":false}),makeQuery(id+"F4.opExtrude","CAP_FACE",FACE,{"disambiguationData":[OSD([subQ0,sQuery(id+"F0.wireOp",EDGE,"E10"),sQuery(id+"F0.wireOp",EDGE,"E12.bottom"),sQuery(id+"F0.wireOp",EDGE,"E12.top"),sQuery(id+"F0.wireOp",EDGE,"E12.left")])],"isStart":false})]});var subQ2=sQuery(id+"F10.wireOp",EDGE,"E21");Q0=makeQuery(id+"F17.opFillet","BLEND_EDGE",EDGE,{"blendedFrom":[makeQuery(id+"F16.opChamfer","BLEND_EDGE",EDGE,{"disambiguationData":[OD(1.0)],"blendedFrom":[makeQuery(id+"F12.boolean.opBoolean","INTERSECT",EDGE,{"derivedFrom":[subQ1,makeQuery(id+"F12.opExtrude","CAP_FACE",FACE,{"disambiguationData":[OSD([subQ2,sQuery(id+"F10.wireOp",EDGE,"E24")])],"isStart":false})]}),makeQuery(id+"F12.boolean.opBoolean","COPY",FACE,{"derivedFrom":makeQuery(id+"F12.opExtrude","SWEPT_FACE",FACE,{"disambiguationData":[OSD([subQ2])]})})],"blendedInto":[makeQuery(id+"F12.boolean.opBoolean","COPY",FACE,{"derivedFrom":makeQuery(id+"F12.opExtrude","SWEPT_FACE",FACE,{"disambiguationData":[OSD([subQ2])]})})]}),subQ1],"blendedInto":[subQ1]});}
            var Q1;
            {var subQ0=sQuery(id+"F0.wireOp",EDGE,"E12.left");var subQ1=sQuery(id+"F0.wireOp",EDGE,"E12.top");var subQ2=sQuery(id+"F0.wireOp",EDGE,"E12.bottom");var subQ3=sQuery(id+"F0.wireOp",EDGE,"E10");var subQ4=sQuery(id+"F0.wireOp",EDGE,"E2");var subQ5=sQuery(id+"F0.wireOp",EDGE,"E8");var subQ6=sQuery(id+"F0.wireOp",EDGE,"E7");var subQ7=sQuery(id+"F0.wireOp",EDGE,"E4");var subQ8=sQuery(id+"F0.wireOp",EDGE,"E1");var subQ9=makeQuery(id+"F4.boolean.opBoolean","MERGE",FACE,{"derivedFrom":[makeQuery(id+"F2.opExtrude","CAP_FACE",FACE,{"disambiguationData":[OSD([subQ8,subQ4])],"isStart":false}),makeQuery(id+"F4.opExtrude","CAP_FACE",FACE,{"disambiguationData":[OSD([subQ4,subQ7,subQ6,subQ5])],"isStart":false}),makeQuery(id+"F4.opExtrude","CAP_FACE",FACE,{"disambiguationData":[OSD([subQ4,subQ3,subQ2,subQ1,subQ0])],"isStart":false})]});var subQ10=sQuery(id+"F10.wireOp",EDGE,"E21");Q1=makeQuery(id+"F17.opFillet","BLEND_EDGE",EDGE,{"blendedFrom":[makeQuery(id+"F16.opChamfer","BLEND_EDGE",EDGE,{"blendedFrom":[makeQuery(id+"F12.boolean.opBoolean","INTERSECT",EDGE,{"derivedFrom":[subQ9,makeQuery(id+"F12.opExtrude","CAP_FACE",FACE,{"disambiguationData":[OSD([subQ10,sQuery(id+"F10.wireOp",EDGE,"E24")])],"isStart":false})]}),makeQuery(id+"F15.opFillet","BLEND_FACE",FACE,{"disambiguationData":[OSD([subQ8,subQ4,subQ7,subQ6,subQ5,subQ3,subQ2,subQ1,subQ0,subQ10])]})],"blendedInto":[makeQuery(id+"F15.opFillet","BLEND_FACE",FACE,{"disambiguationData":[OSD([subQ8,subQ4,subQ7,subQ6,subQ5,subQ3,subQ2,subQ1,subQ0,subQ10])]})]}),subQ9],"blendedInto":[subQ9]});}
            fillet(context, id + "F27", {"entities" : qUnion([Q0, Q1]), "radius" : 5 * mm, "tangentPropagation" : true, "allowEdgeOverflow" : false});
        }
        {
            var Q0;
            {var subQ0=sQuery(id+"F10.wireOp",EDGE,"E22");var subQ2=sQuery(id+"F0.wireOp",EDGE,"E7");var subQ4=sQuery(id+"F0.wireOp",EDGE,"E2");var subQ9=sQuery(id+"F0.wireOp",EDGE,"E5");var subQ10=sQuery(id+"F0.wireOp",EDGE,"E3");var subQ12=makeQuery(id+"F0.imprint","INTERSECT",VERTEX,{"derivedFrom":[subQ4,subQ9]});var subQ13=makeQuery(id+"F0.imprint","INTERSECT",VERTEX,{"derivedFrom":[subQ4,subQ10]});Q0=makeQuery(id+"F13.boolean.opBoolean","INTERSECT",EDGE,{"derivedFrom":[makeQuery(id+"F12.boolean.opBoolean","SPLIT",FACE,{"disambiguationData":[TD([makeQuery(id+"F3.opExtrude","SWEPT_FACE",FACE,{"disambiguationData":[OSD([subQ2])]})])],"derivedFrom":makeQuery(id+"F9.boolean.opBoolean","MERGE",FACE,{"derivedFrom":[makeQuery(id+"F8.boolean.opBoolean","MERGE",FACE,{"derivedFrom":[makeQuery(id+"F3.opExtrude","SWEPT_FACE",FACE,{"disambiguationData":[OSD([subQ4]),TDD([makeQuery(id+"F0.imprint","IMPRINT",EDGE,{"disambiguationData":[TD([[subQ13,1.0]])],"derivedFrom":subQ4}),makeQuery(id+"F0.imprint","IMPRINT",EDGE,{"disambiguationData":[TD([[subQ13,-1.0]])],"derivedFrom":subQ4})])]}),makeQuery(id+"F3.opExtrude","SWEPT_FACE",FACE,{"disambiguationData":[OSD([subQ4]),TDD([makeQuery(id+"F0.imprint","IMPRINT",EDGE,{"disambiguationData":[TD([[subQ12,1.0]])],"derivedFrom":subQ4}),makeQuery(id+"F0.imprint","IMPRINT",EDGE,{"disambiguationData":[TD([[subQ12,-1.0]])],"derivedFrom":subQ4})])]}),makeQuery(id+"F8.opExtrude","SWEPT_FACE",FACE,{"disambiguationData":[OSD([subQ4])]})]}),makeQuery(id+"F9.opExtrude","SWEPT_FACE",FACE,{"disambiguationData":[OSD([subQ4])]})]})}),makeQuery(id+"F13.opExtrude","SWEPT_FACE",FACE,{"disambiguationData":[OSD([subQ0])]})]});}
            fillet(context, id + "F28", {"entities" : qUnion([Q0]), "radius" : 13.3 * mm, "tangentPropagation" : true, "allowEdgeOverflow" : false});
        }
    });
